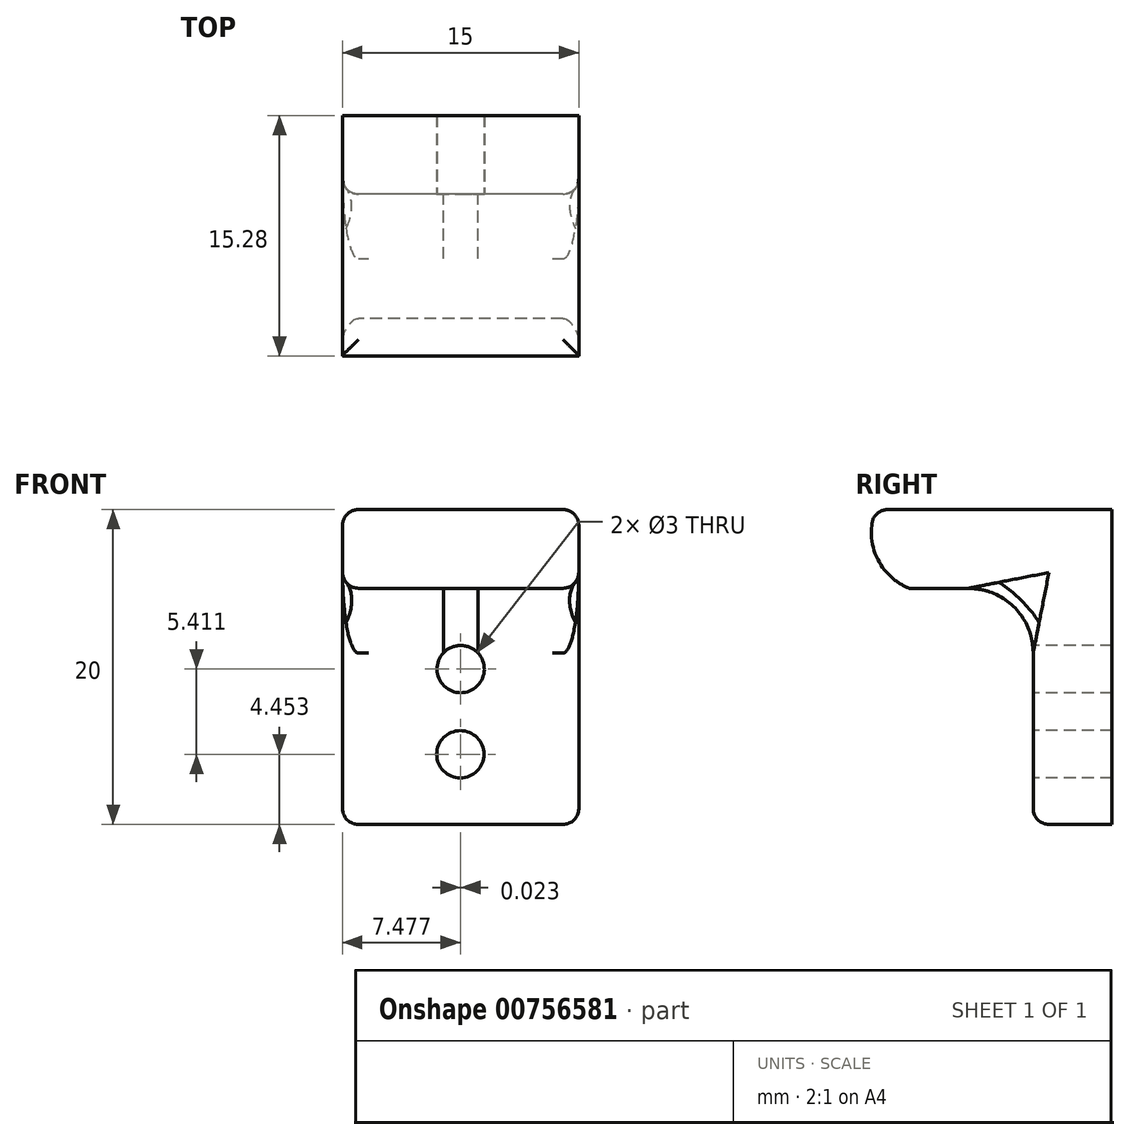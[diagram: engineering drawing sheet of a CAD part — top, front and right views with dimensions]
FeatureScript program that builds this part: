
annotation { "Feature Type Name" : "Feature", "Feature Type Description" : "" }
export const myFeature = defineFeature(function(context is Context, id is Id, definition is map)
    precondition{}
    {
        {
            var Q0;
            Q0=qCreatedBy(makeId("Right.planeOp"),FACE);
            var sketch = newSketch(context, id + "F0", { "sketchPlane" : qUnion([Q0])});
            skLineSegment(sketch, "E0", {"start": v(-9.3, 5.25) * mm, "end": v(5.7, 5.25) * mm});
            skLineSegment(sketch, "E1", {"start": v(5.7, 5.25) * mm, "end": v(5.7, -14.75) * mm});
            skLineSegment(sketch, "E2", {"start": v(5.7, -14.75) * mm, "end": v(0.7, -14.75) * mm});
            skLineSegment(sketch, "E3", {"start": v(0.7, -14.75) * mm, "end": v(0.7, 0.25) * mm});
            skLineSegment(sketch, "E4", {"start": v(0.7, 0.25) * mm, "end": v(-7.19, 0.25) * mm});
            skArc(sketch, "E5", {"start": v(-9.3, 5.25) * mm, "mid": v(-9.27, 2.31) * mm, "end": v(-7.19, 0.25) * mm});
            skSolve(sketch);
        }
        {
            var Q0;
            Q0 = qSketchRegion(id + "F0", true);
            extrude(context, id + "F1", {"entities" : qUnion([Q0]), "depth" : 7.5 * mm, "offsetDistance" : 25 * mm, "hasSecondDirection" : true, "secondDirectionOppositeDirection" : true, "secondDirectionDepth" : 7.5 * mm});
        }
        {
            var Q0;
            Q0=makeQuery(id+"F1.opExtrude","SWEPT_FACE",FACE,{"disambiguationData":[OSD([sQuery(id+"F0.wireOp",EDGE,"E3")])]});
            var sketch = newSketch(context, id + "F2", { "sketchPlane" : qUnion([Q0])});
            skCircle(sketch, "E6", {"center": v(0, -4.89) * mm, "radius": 1.5 * mm});
            skCircle(sketch, "E7", {"center": v(-0.02, -10.3) * mm, "radius": 1.5 * mm});
            skSolve(sketch);
        }
        {
            var Q0;
            Q0 = qSketchRegion(id + "F2", true);
            extrude(context, id + "F3", {"entities" : qUnion([Q0]), "operationType" : NewBodyOperationType.REMOVE, "endBound" : BoundingType.THROUGH_ALL, "oppositeDirection" : true, "depth" : 25 * mm, "offsetDistance" : 25 * mm});
        }
        {
            var Q0;
            Q0=makeQuery(id+"F1.opExtrude","CAP_EDGE",EDGE,{"disambiguationData":[OSD([sQuery(id+"F0.wireOp",EDGE,"E0")])],"isStart":false});
            var Q1;
            Q1=makeQuery(id+"F1.opExtrude","CAP_EDGE",EDGE,{"disambiguationData":[OSD([sQuery(id+"F0.wireOp",EDGE,"E0")])],"isStart":true});
            var Q2;
            Q2=makeQuery(id+"F1.opExtrude","SWEPT_EDGE",EDGE,{"disambiguationData":[OSD([sQuery(id+"F0.wireOp",EDGE,"E0"),sQuery(id+"F0.wireOp",EDGE,"E5")])]});
            var Q3;
            Q3=makeQuery(id+"F1.opExtrude","CAP_EDGE",EDGE,{"disambiguationData":[OSD([sQuery(id+"F0.wireOp",EDGE,"E2")])],"isStart":false});
            var Q4;
            Q4=makeQuery(id+"F1.opExtrude","SWEPT_EDGE",EDGE,{"disambiguationData":[OSD([sQuery(id+"F0.wireOp",EDGE,"E2"),sQuery(id+"F0.wireOp",EDGE,"E3")])]});
            var Q5;
            Q5=makeQuery(id+"F1.opExtrude","CAP_EDGE",EDGE,{"disambiguationData":[OSD([sQuery(id+"F0.wireOp",EDGE,"E2")])],"isStart":true});
            var Q6;
            Q6=makeQuery(id+"F1.opExtrude","CAP_EDGE",EDGE,{"disambiguationData":[OSD([sQuery(id+"F0.wireOp",EDGE,"E3")])],"isStart":false});
            var Q7;
            Q7=makeQuery(id+"F1.opExtrude","CAP_EDGE",EDGE,{"disambiguationData":[OSD([sQuery(id+"F0.wireOp",EDGE,"E4")])],"isStart":true});
            var Q8;
            Q8=makeQuery(id+"F1.opExtrude","CAP_EDGE",EDGE,{"disambiguationData":[OSD([sQuery(id+"F0.wireOp",EDGE,"E3")])],"isStart":true});
            var Q9;
            Q9=makeQuery(id+"F1.opExtrude","CAP_EDGE",EDGE,{"disambiguationData":[OSD([sQuery(id+"F0.wireOp",EDGE,"E4")])],"isStart":false});
            fillet(context, id + "F4", {"entities" : qUnion([Q0, Q1, Q2, Q3, Q4, Q5, Q6, Q7, Q8, Q9]), "radius" : 1 * mm, "tangentPropagation" : true, "allowEdgeOverflow" : false});
        }
        {
            var Q0;
            Q0=makeQuery(id+"F1.opExtrude","SWEPT_EDGE",EDGE,{"disambiguationData":[OSD([sQuery(id+"F0.wireOp",EDGE,"E3"),sQuery(id+"F0.wireOp",EDGE,"E4")])]});
            fillet(context, id + "F5", {"entities" : qUnion([Q0]), "radius" : 4.1 * mm, "tangentPropagation" : true, "allowEdgeOverflow" : false});
        }
    });
